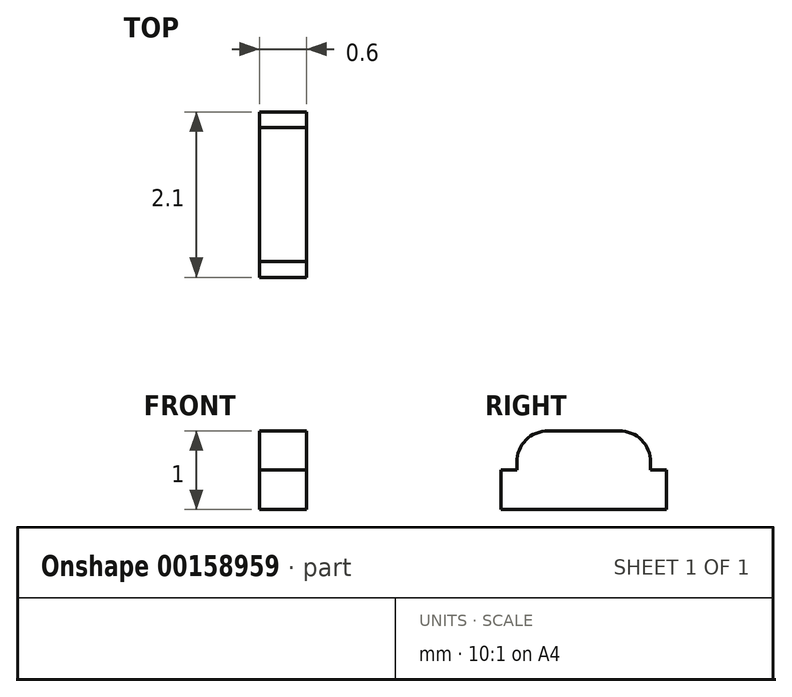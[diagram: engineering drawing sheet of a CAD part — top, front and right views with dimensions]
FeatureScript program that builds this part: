
annotation { "Feature Type Name" : "Feature", "Feature Type Description" : "" }
export const myFeature = defineFeature(function(context is Context, id is Id, definition is map)
    precondition{}
    {
        {
            var Q0;
            Q0=qCreatedBy(makeId("Top.planeOp"),FACE);
            var sketch = newSketch(context, id + "F0", { "sketchPlane" : qUnion([Q0])});
            skLineSegment(sketch, "E0.bottom", {"start": v(0.3, 1.05) * mm, "end": v(-0.3, 1.05) * mm});
            skLineSegment(sketch, "E0.top", {"start": v(0.3, -1.05) * mm, "end": v(-0.3, -1.05) * mm});
            skLineSegment(sketch, "E0.left", {"start": v(0.3, 1.05) * mm, "end": v(0.3, -1.05) * mm});
            skLineSegment(sketch, "E0.right", {"start": v(-0.3, 1.05) * mm, "end": v(-0.3, -1.05) * mm});
            skPoint(sketch, "E0.middle", {"position": v(0, 0) * mm});
            skLineSegment(sketch, "E1.bottom", {"start": v(-0.3, 0.85) * mm, "end": v(0.3, 0.85) * mm});
            skLineSegment(sketch, "E1.top", {"start": v(-0.3, -0.85) * mm, "end": v(0.3, -0.85) * mm});
            skLineSegment(sketch, "E1.left", {"start": v(-0.3, 0.85) * mm, "end": v(-0.3, -0.85) * mm});
            skLineSegment(sketch, "E1.right", {"start": v(0.3, 0.85) * mm, "end": v(0.3, -0.85) * mm});
            skSolve(sketch);
        }
        {
            var Q0;
            Q0=makeQuery(id+"F0.imprint","IMPRINT",FACE,{"disambiguationData":[TD([[makeQuery(id+"F0.imprint","IMPRINT",EDGE,{"derivedFrom":sQuery(id+"F0.wireOp",EDGE,"E1.bottom")}),-1.0]])]});
            var Q1;
            {var subQ0=sQuery(id+"F0.wireOp",EDGE,"E0.top");Q1=makeQuery(id+"F0.imprint","IMPRINT",FACE,{"disambiguationData":[TD([[makeQuery(id+"F0.imprint","IMPRINT",EDGE,{"derivedFrom":subQ0}),-1.0]])]});}
            var Q2;
            {var subQ0=sQuery(id+"F0.wireOp",EDGE,"E0.bottom");Q2=makeQuery(id+"F0.imprint","IMPRINT",FACE,{"disambiguationData":[TD([[makeQuery(id+"F0.imprint","IMPRINT",EDGE,{"derivedFrom":subQ0}),1.0]])]});}
            extrude(context, id + "F1", {"entities" : qUnion([Q0, Q1, Q2]), "oppositeDirection" : true, "depth" : 0.5 * mm});
        }
        {
            var Q0;
            Q0=makeQuery(id+"F0.imprint","IMPRINT",FACE,{"disambiguationData":[TD([[makeQuery(id+"F0.imprint","IMPRINT",EDGE,{"derivedFrom":sQuery(id+"F0.wireOp",EDGE,"E1.bottom")}),-1.0]])]});
            extrude(context, id + "F2", {"entities" : qUnion([Q0]), "operationType" : NewBodyOperationType.ADD, "depth" : 0.5 * mm});
        }
        {
            var Q0;
            Q0=makeQuery(id+"F2.opExtrude","CAP_EDGE",EDGE,{"disambiguationData":[OSD([sQuery(id+"F0.wireOp",EDGE,"E1.top")])],"isStart":false});
            var Q1;
            Q1=makeQuery(id+"F2.opExtrude","CAP_EDGE",EDGE,{"disambiguationData":[OSD([sQuery(id+"F0.wireOp",EDGE,"E1.bottom")])],"isStart":false});
            fillet(context, id + "F3", {"entities" : qUnion([Q0, Q1]), "radius" : 0.4 * mm, "tangentPropagation" : true, "allowEdgeOverflow" : false});
        }
    });
